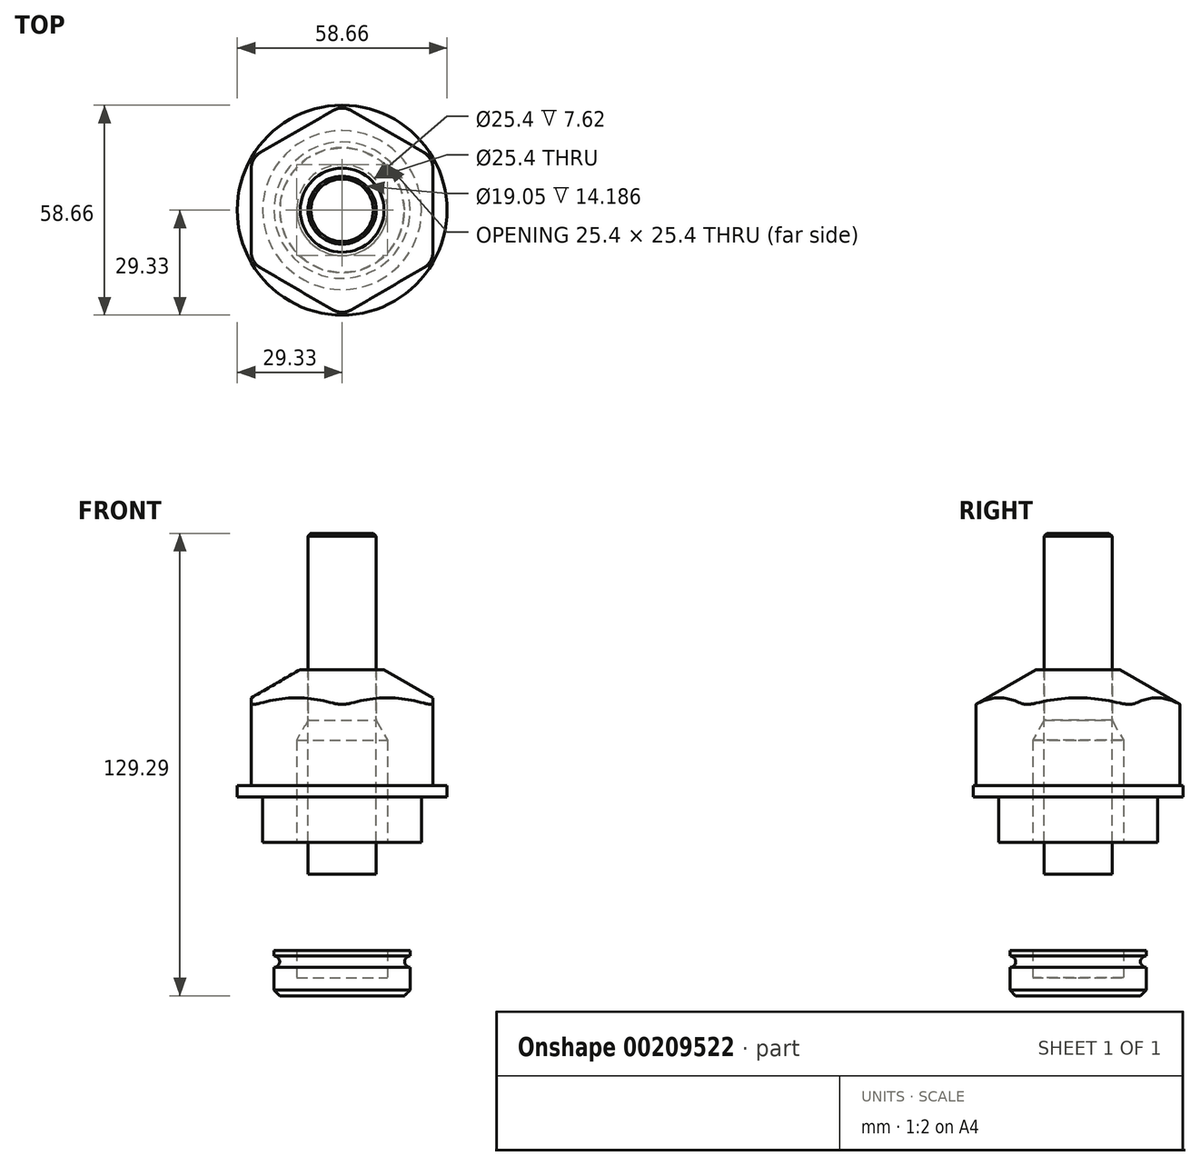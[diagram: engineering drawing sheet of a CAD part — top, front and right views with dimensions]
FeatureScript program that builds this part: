
annotation { "Feature Type Name" : "Feature", "Feature Type Description" : "" }
export const myFeature = defineFeature(function(context is Context, id is Id, definition is map)
    precondition{}
    {
        {
            var Q0;
            Q0=qCreatedBy(makeId("Top.planeOp"),FACE);
            var sketch = newSketch(context, id + "F0", { "sketchPlane" : qUnion([Q0])});
            skCircle(sketch, "E0", {"center": v(0, 0) * mm, "radius": 29.33 * mm});
            skLineSegment(sketch, "E1", {"start": v(0, 29.33) * mm, "end": v(0, -29.33) * mm, "construction": true});
            skLineSegment(sketch, "E2", {"start": v(-25.4, 14.66) * mm, "end": v(25.4, -14.66) * mm, "construction": true});
            skLineSegment(sketch, "E3", {"start": v(-25.4, -14.66) * mm, "end": v(25.4, 14.66) * mm, "construction": true});
            skLineSegment(sketch, "E4", {"start": v(-25.4, 14.66) * mm, "end": v(0, 29.33) * mm});
            skLineSegment(sketch, "E5", {"start": v(0, 29.33) * mm, "end": v(25.4, 14.66) * mm});
            skLineSegment(sketch, "E6", {"start": v(25.4, 14.66) * mm, "end": v(25.4, -14.66) * mm});
            skLineSegment(sketch, "E7", {"start": v(25.4, -14.66) * mm, "end": v(0, -29.33) * mm});
            skLineSegment(sketch, "E8", {"start": v(0, -29.33) * mm, "end": v(-25.4, -14.66) * mm});
            skLineSegment(sketch, "E9", {"start": v(-25.4, -14.66) * mm, "end": v(-25.4, 14.66) * mm});
            skCircle(sketch, "E10", {"center": v(0, 0) * mm, "radius": 7.94 * mm});
            skSolve(sketch);
        }
        {
            var Q0;
            Q0=makeQuery(id+"F0.imprint","IMPRINT",FACE,{"disambiguationData":[TD([[makeQuery(id+"F0.imprint","IMPRINT",EDGE,{"derivedFrom":sQuery(id+"F0.wireOp",EDGE,"E10")}),1.0]])]});
            var Q1;
            Q1=makeQuery(id+"F0.imprint","IMPRINT",FACE,{"disambiguationData":[TD([[makeQuery(id+"F0.imprint","IMPRINT",EDGE,{"derivedFrom":sQuery(id+"F0.wireOp",EDGE,"E4")}),-1.0]])]});
            extrude(context, id + "F1", {"entities" : qUnion([Q0, Q1]), "depth" : 35.56 * mm});
        }
        {
            var Q0;
            {var subQ0=sQuery(id+"F0.wireOp",EDGE,"E8");Q0=makeQuery(id+"F0.imprint","IMPRINT",FACE,{"disambiguationData":[TD([[makeQuery(id+"F0.imprint","IMPRINT",EDGE,{"derivedFrom":subQ0}),1.0]])]});}
            var Q1;
            {var subQ0=sQuery(id+"F0.wireOp",EDGE,"E7");Q1=makeQuery(id+"F0.imprint","IMPRINT",FACE,{"disambiguationData":[TD([[makeQuery(id+"F0.imprint","IMPRINT",EDGE,{"derivedFrom":subQ0}),1.0]])]});}
            var Q2;
            {var subQ0=sQuery(id+"F0.wireOp",EDGE,"E6");Q2=makeQuery(id+"F0.imprint","IMPRINT",FACE,{"disambiguationData":[TD([[makeQuery(id+"F0.imprint","IMPRINT",EDGE,{"derivedFrom":subQ0}),1.0]])]});}
            var Q3;
            Q3=makeQuery(id+"F0.imprint","IMPRINT",FACE,{"disambiguationData":[TD([[makeQuery(id+"F0.imprint","IMPRINT",EDGE,{"derivedFrom":sQuery(id+"F0.wireOp",EDGE,"E4")}),-1.0]])]});
            var Q4;
            {var subQ0=sQuery(id+"F0.wireOp",EDGE,"E5");Q4=makeQuery(id+"F0.imprint","IMPRINT",FACE,{"disambiguationData":[TD([[makeQuery(id+"F0.imprint","IMPRINT",EDGE,{"derivedFrom":subQ0}),1.0]])]});}
            var Q5;
            {var subQ0=sQuery(id+"F0.wireOp",EDGE,"E4");Q5=makeQuery(id+"F0.imprint","IMPRINT",FACE,{"disambiguationData":[TD([[makeQuery(id+"F0.imprint","IMPRINT",EDGE,{"derivedFrom":subQ0}),1.0]])]});}
            var Q6;
            {var subQ0=sQuery(id+"F0.wireOp",EDGE,"E9");Q6=makeQuery(id+"F0.imprint","IMPRINT",FACE,{"disambiguationData":[TD([[makeQuery(id+"F0.imprint","IMPRINT",EDGE,{"derivedFrom":subQ0}),1.0]])]});}
            extrude(context, id + "F2", {"entities" : qUnion([Q0, Q1, Q2, Q3, Q4, Q5, Q6]), "operationType" : NewBodyOperationType.ADD, "depth" : 3.17 * mm});
        }
        {
            var Q0;
            Q0=makeQuery(id+"F1.opExtrude","SWEPT_EDGE",EDGE,{"disambiguationData":[OSD([sQuery(id+"F0.wireOp",EDGE,"E0"),sQuery(id+"F0.wireOp",EDGE,"E7"),sQuery(id+"F0.wireOp",EDGE,"E8")])]});
            var Q1;
            Q1=makeQuery(id+"F1.opExtrude","SWEPT_EDGE",EDGE,{"disambiguationData":[OSD([sQuery(id+"F0.wireOp",EDGE,"E0"),sQuery(id+"F0.wireOp",EDGE,"E6"),sQuery(id+"F0.wireOp",EDGE,"E7")])]});
            var Q2;
            Q2=makeQuery(id+"F1.opExtrude","SWEPT_EDGE",EDGE,{"disambiguationData":[OSD([sQuery(id+"F0.wireOp",EDGE,"E0"),sQuery(id+"F0.wireOp",EDGE,"E5"),sQuery(id+"F0.wireOp",EDGE,"E6")])]});
            var Q3;
            Q3=makeQuery(id+"F1.opExtrude","SWEPT_EDGE",EDGE,{"disambiguationData":[OSD([sQuery(id+"F0.wireOp",EDGE,"E0"),sQuery(id+"F0.wireOp",EDGE,"E4"),sQuery(id+"F0.wireOp",EDGE,"E5")])]});
            var Q4;
            Q4=makeQuery(id+"F1.opExtrude","SWEPT_EDGE",EDGE,{"disambiguationData":[OSD([sQuery(id+"F0.wireOp",EDGE,"E0"),sQuery(id+"F0.wireOp",EDGE,"E4"),sQuery(id+"F0.wireOp",EDGE,"E9")])]});
            var Q5;
            Q5=makeQuery(id+"F1.opExtrude","SWEPT_EDGE",EDGE,{"disambiguationData":[OSD([sQuery(id+"F0.wireOp",EDGE,"E0"),sQuery(id+"F0.wireOp",EDGE,"E8"),sQuery(id+"F0.wireOp",EDGE,"E9")])]});
            fillet(context, id + "F3", {"entities" : qUnion([Q0, Q1, Q2, Q3, Q4, Q5]), "radius" : 5.08 * mm, "tangentPropagation" : true, "allowEdgeOverflow" : false});
        }
        {
            var Q0;
            Q0=qCreatedBy(makeId("Right.planeOp"),FACE);
            var sketch = newSketch(context, id + "F4", { "sketchPlane" : qUnion([Q0])});
            skLineSegment(sketch, "E11", {"start": v(0, 52) * mm, "end": v(0, 0) * mm, "construction": true});
            skLineSegment(sketch, "E12", {"start": v(11.73, 35.56) * mm, "end": v(35.4, 21.9) * mm});
            skLineSegment(sketch, "E13", {"start": v(35.4, 21.9) * mm, "end": v(35.4, 35.56) * mm});
            skLineSegment(sketch, "E14", {"start": v(35.4, 35.56) * mm, "end": v(11.73, 35.56) * mm});
            skLineSegment(sketch, "E15.0", {"start": v(11.73, 35.56) * mm, "end": v(-11.73, 35.56) * mm});
            skLineSegment(sketch, "E16.bottom", {"start": v(0, 0) * mm, "end": v(22.23, 0) * mm});
            skLineSegment(sketch, "E16.top", {"start": v(0, -12.7) * mm, "end": v(22.23, -12.7) * mm});
            skLineSegment(sketch, "E16.left", {"start": v(0, 0) * mm, "end": v(0, -12.7) * mm});
            skLineSegment(sketch, "E16.right", {"start": v(22.23, 0) * mm, "end": v(22.23, -12.7) * mm});
            skLineSegment(sketch, "E17.bottom", {"start": v(0, -12.7) * mm, "end": v(19.05, -12.7) * mm});
            skLineSegment(sketch, "E17.top", {"start": v(0, -27.69) * mm, "end": v(19.05, -27.69) * mm});
            skLineSegment(sketch, "E17.left", {"start": v(0, -12.7) * mm, "end": v(0, -27.69) * mm});
            skLineSegment(sketch, "E17.right", {"start": v(19.05, -12.7) * mm, "end": v(19.05, -27.69) * mm});
            skLineSegment(sketch, "E18.bottom", {"start": v(17.78, -27.69) * mm, "end": v(0, -27.69) * mm});
            skLineSegment(sketch, "E18.top", {"start": v(17.78, -42.93) * mm, "end": v(0, -42.93) * mm});
            skLineSegment(sketch, "E18.left", {"start": v(17.78, -27.69) * mm, "end": v(17.78, -42.93) * mm});
            skLineSegment(sketch, "E18.right", {"start": v(0, -27.69) * mm, "end": v(0, -42.93) * mm});
            skLineSegment(sketch, "E19.bottom", {"start": v(0, -42.93) * mm, "end": v(19.05, -42.93) * mm});
            skLineSegment(sketch, "E19.top", {"start": v(0, -55.63) * mm, "end": v(19.05, -55.63) * mm});
            skLineSegment(sketch, "E19.left", {"start": v(0, -42.93) * mm, "end": v(0, -55.63) * mm});
            skLineSegment(sketch, "E19.right", {"start": v(19.05, -42.93) * mm, "end": v(19.05, -55.63) * mm});
            skCircle(sketch, "E20", {"center": v(19.05, -24.51) * mm, "radius": 1.59 * mm});
            skCircle(sketch, "E21", {"center": v(19.05, -46.1) * mm, "radius": 1.59 * mm});
            skCircle(sketch, "E22", {"center": v(0, -17.46) * mm, "radius": 3.18 * mm});
            skCircle(sketch, "E23", {"center": v(0, -35.3) * mm, "radius": 3.18 * mm});
            skSolve(sketch);
        }
        {
            var Q0;
            Q0=makeQuery(id+"F4.imprint","IMPRINT",FACE,{"disambiguationData":[TD([[makeQuery(id+"F4.imprint","IMPRINT",EDGE,{"derivedFrom":sQuery(id+"F4.wireOp",EDGE,"E12")}),1.0]])]});
            var Q1;
            Q1=sQuery(id+"F4.wireOp",EDGE,"E11");
            revolve(context, id + "F5", {"operationType" : NewBodyOperationType.REMOVE, "entities" : qUnion([Q0]), "axis" : qUnion([Q1]), "revolveType" : RevolveType.FULL, "oppositeDirection" : true});
        }
        {
            var Q0;
            {var subQ7=sQuery(id+"F4.wireOp",EDGE,"E18.bottom");Q0=makeQuery(id+"F4.imprint","IMPRINT",FACE,{"disambiguationData":[TD([[makeQuery(id+"F4.imprint","IMPRINT",EDGE,{"derivedFrom":subQ7}),1.0]])]});}
            var Q1;
            {var subQ10=sQuery(id+"F4.wireOp",EDGE,"E17.bottom");Q1=makeQuery(id+"F4.imprint","IMPRINT",FACE,{"disambiguationData":[TD([[makeQuery(id+"F4.imprint","IMPRINT",EDGE,{"derivedFrom":subQ10}),-1.0]])]});}
            var Q2;
            Q2=makeQuery(id+"F4.imprint","IMPRINT",FACE,{"disambiguationData":[TD([[makeQuery(id+"F4.imprint","IMPRINT",EDGE,{"derivedFrom":sQuery(id+"F4.wireOp",EDGE,"E16.bottom")}),-1.0]])]});
            var Q3;
            {var subQ4=sQuery(id+"F4.wireOp",EDGE,"E19.top");Q3=makeQuery(id+"F4.imprint","IMPRINT",FACE,{"disambiguationData":[TD([[makeQuery(id+"F4.imprint","IMPRINT",EDGE,{"derivedFrom":subQ4}),1.0]])]});}
            var Q4;
            Q4=sQuery(id+"F4.wireOp",EDGE,"E11");
            revolve(context, id + "F6", {"operationType" : NewBodyOperationType.ADD, "entities" : qUnion([Q0, Q1, Q2, Q3]), "axis" : qUnion([Q4]), "revolveType" : RevolveType.FULL});
        }
        {
            var Q0;
            Q0=makeQuery(id+"F6.opRevolve","SWEPT_EDGE",EDGE,{"disambiguationData":[OSD([sQuery(id+"F4.wireOp",EDGE,"E19.top"),sQuery(id+"F4.wireOp",EDGE,"E19.right")])]});
            chamfer(context, id + "F7", {"entities" : qUnion([Q0]), "width" : 1.59 * mm, "tangentPropagation" : true});
        }
        {
            var Q0;
            {var subQ0=sQuery(id+"F4.wireOp",EDGE,"E16.right");var subQ1=sQuery(id+"F4.wireOp",EDGE,"E20");var subQ3=makeQuery(id+"F4.imprint","INTERSECT",VERTEX,{"disambiguationData":[OD(0.0)],"derivedFrom":[subQ0,subQ1]});Q0=makeQuery(id+"F4.imprint","IMPRINT",FACE,{"disambiguationData":[TD([[makeQuery(id+"F4.imprint","SKETCH_ENTITY",EDGE,{"disambiguationData":[TD([[subQ3,-1.0]])],"sketchEntityId":"E16.right"}),1.0]])]});}
            var Q1;
            {var subQ0=sQuery(id+"F4.wireOp",EDGE,"E20");var subQ1=sQuery(id+"F4.wireOp",EDGE,"E17.right");var subQ3=makeQuery(id+"F4.imprint","INTERSECT",VERTEX,{"disambiguationData":[OD(0.0)],"derivedFrom":[subQ1,subQ0]});Q1=makeQuery(id+"F4.imprint","IMPRINT",FACE,{"disambiguationData":[TD([[makeQuery(id+"F4.imprint","IMPRINT",EDGE,{"disambiguationData":[TD([[subQ3,-1.0]])],"derivedFrom":subQ1}),-1.0]])]});}
            var Q2;
            {var subQ0=sQuery(id+"F4.wireOp",EDGE,"E20");var subQ1=sQuery(id+"F4.wireOp",EDGE,"E17.right");var subQ3=makeQuery(id+"F4.imprint","INTERSECT",VERTEX,{"disambiguationData":[OD(0.0)],"derivedFrom":[subQ1,subQ0]});Q2=makeQuery(id+"F4.imprint","IMPRINT",FACE,{"disambiguationData":[TD([[makeQuery(id+"F4.imprint","IMPRINT",EDGE,{"disambiguationData":[TD([[subQ3,-1.0]])],"derivedFrom":subQ1}),1.0]])]});}
            var Q3;
            Q3=sQuery(id+"F4.wireOp",EDGE,"E11");
            revolve(context, id + "F8", {"entities" : qUnion([Q0, Q1, Q2]), "axis" : qUnion([Q3]), "revolveType" : RevolveType.FULL});
        }
        {
            var Q0;
            {var subQ0=sQuery(id+"F4.wireOp",EDGE,"E22");var subQ1=sQuery(id+"F4.wireOp",EDGE,"E17.left");var subQ3=makeQuery(id+"F4.imprint","INTERSECT",VERTEX,{"disambiguationData":[OD(0.0)],"derivedFrom":[subQ1,subQ0]});Q0=makeQuery(id+"F4.imprint","IMPRINT",FACE,{"disambiguationData":[TD([[makeQuery(id+"F4.imprint","IMPRINT",EDGE,{"disambiguationData":[TD([[subQ3,-1.0]])],"derivedFrom":subQ1}),-1.0]])]});}
            var Q1;
            {var subQ0=sQuery(id+"F4.wireOp",EDGE,"E22");var subQ1=sQuery(id+"F4.wireOp",EDGE,"E17.left");var subQ3=makeQuery(id+"F4.imprint","INTERSECT",VERTEX,{"disambiguationData":[OD(0.0)],"derivedFrom":[subQ1,subQ0]});Q1=makeQuery(id+"F4.imprint","IMPRINT",FACE,{"disambiguationData":[TD([[makeQuery(id+"F4.imprint","IMPRINT",EDGE,{"disambiguationData":[TD([[subQ3,-1.0]])],"derivedFrom":subQ1}),1.0]])]});}
            var Q2;
            {var subQ0=sQuery(id+"F4.wireOp",EDGE,"E23");var subQ1=sQuery(id+"F4.wireOp",EDGE,"E18.right");var subQ3=makeQuery(id+"F4.imprint","INTERSECT",VERTEX,{"disambiguationData":[OD(0.0)],"derivedFrom":[subQ1,subQ0]});Q2=makeQuery(id+"F4.imprint","IMPRINT",FACE,{"disambiguationData":[TD([[makeQuery(id+"F4.imprint","IMPRINT",EDGE,{"disambiguationData":[TD([[subQ3,-1.0]])],"derivedFrom":subQ1}),-1.0]])]});}
            var Q3;
            {var subQ0=sQuery(id+"F4.wireOp",EDGE,"E23");var subQ1=sQuery(id+"F4.wireOp",EDGE,"E18.right");var subQ3=makeQuery(id+"F4.imprint","INTERSECT",VERTEX,{"disambiguationData":[OD(0.0)],"derivedFrom":[subQ1,subQ0]});Q3=makeQuery(id+"F4.imprint","IMPRINT",FACE,{"disambiguationData":[TD([[makeQuery(id+"F4.imprint","IMPRINT",EDGE,{"disambiguationData":[TD([[subQ3,-1.0]])],"derivedFrom":subQ1}),1.0]])]});}
            extrude(context, id + "F9", {"entities" : qUnion([Q0, Q1, Q2, Q3]), "operationType" : NewBodyOperationType.REMOVE, "endBound" : BoundingType.THROUGH_ALL, "depth" : 25.4 * mm});
        }
        {
            var Q0;
            Q0=qCreatedBy(makeId("Right.planeOp"),FACE);
            var sketch = newSketch(context, id + "F10", { "sketchPlane" : qUnion([Q0])});
            skLineSegment(sketch, "E24", {"start": v(0, 73.66) * mm, "end": v(0, -50.55) * mm});
            skLineSegment(sketch, "E25", {"start": v(0, -50.55) * mm, "end": v(12.7, -50.55) * mm});
            skLineSegment(sketch, "E26", {"start": v(12.7, -50.55) * mm, "end": v(12.7, 15.88) * mm});
            skLineSegment(sketch, "E27", {"start": v(12.7, 15.88) * mm, "end": v(0, 15.88) * mm});
            skLineSegment(sketch, "E28", {"start": v(9.53, -21.6) * mm, "end": v(9.53, 73.66) * mm});
            skLineSegment(sketch, "E29", {"start": v(9.52, 73.66) * mm, "end": v(0, 73.66) * mm});
            skLineSegment(sketch, "E30", {"start": v(9.53, 21.37) * mm, "end": v(12.7, 15.88) * mm});
            skLineSegment(sketch, "E31.rect.bottom", {"start": v(12.7, -27.94) * mm, "end": v(-12.7, -27.94) * mm});
            skLineSegment(sketch, "E31.rect.top", {"start": v(12.7, -21.59) * mm, "end": v(-12.7, -21.59) * mm});
            skLineSegment(sketch, "E31.rect.left", {"start": v(12.7, -27.94) * mm, "end": v(12.7, -21.59) * mm});
            skLineSegment(sketch, "E31.rect.right", {"start": v(-12.7, -27.94) * mm, "end": v(-12.7, -21.59) * mm});
            skPoint(sketch, "E31.rect.middle", {"position": v(0, -24.77) * mm});
            skSolve(sketch);
        }
        {
            var Q0;
            {var subQ0=sQuery(id+"F10.wireOp",EDGE,"E29");Q0=makeQuery(id+"F10.imprint","IMPRINT",FACE,{"disambiguationData":[TD([[makeQuery(id+"F10.imprint","IMPRINT",EDGE,{"derivedFrom":subQ0}),1.0]])]});}
            var Q1;
            {var subQ0=sQuery(id+"F10.wireOp",EDGE,"E30");Q1=makeQuery(id+"F10.imprint","IMPRINT",FACE,{"disambiguationData":[TD([[makeQuery(id+"F10.imprint","IMPRINT",EDGE,{"derivedFrom":subQ0}),-1.0]])]});}
            var Q2;
            {var subQ1=sQuery(id+"F10.wireOp",EDGE,"E24");var subQ5=sQuery(id+"F10.wireOp",EDGE,"E27");var subQ7=makeQuery(id+"F10.imprint","INTERSECT",VERTEX,{"derivedFrom":[subQ1,subQ5]});Q2=makeQuery(id+"F10.imprint","IMPRINT",FACE,{"disambiguationData":[TD([[makeQuery(id+"F10.imprint","IMPRINT",EDGE,{"disambiguationData":[TD([[subQ7,-1.0]])],"derivedFrom":subQ1}),1.0]])]});}
            var Q3;
            {var subQ0=sQuery(id+"F10.wireOp",EDGE,"E31.rect.top");var subQ3=sQuery(id+"F10.wireOp",EDGE,"E28");var subQ4=makeQuery(id+"F10.imprint","INTERSECT",VERTEX,{"derivedFrom":[subQ3,subQ0]});Q3=makeQuery(id+"F10.imprint","IMPRINT",FACE,{"disambiguationData":[TD([[makeQuery(id+"F10.imprint","IMPRINT",EDGE,{"disambiguationData":[TD([[subQ4,-1.0]])],"derivedFrom":subQ3}),-1.0]])]});}
            var Q4;
            {var subQ5=sQuery(id+"F10.wireOp",EDGE,"E25");Q4=makeQuery(id+"F10.imprint","IMPRINT",FACE,{"disambiguationData":[TD([[makeQuery(id+"F10.imprint","IMPRINT",EDGE,{"derivedFrom":subQ5}),1.0]])]});}
            var Q5;
            {var subQ0=sQuery(id+"F10.wireOp",EDGE,"E31.rect.left");Q5=makeQuery(id+"F10.imprint","IMPRINT",FACE,{"disambiguationData":[TD([[makeQuery(id+"F10.imprint","IMPRINT",EDGE,{"derivedFrom":subQ0}),1.0]])]});}
            var Q6;
            Q6=sQuery(id+"F10.wireOp",EDGE,"E24");
            revolve(context, id + "F11", {"operationType" : NewBodyOperationType.REMOVE, "entities" : qUnion([Q0, Q1, Q2, Q3, Q4, Q5]), "axis" : qUnion([Q6]), "revolveType" : RevolveType.FULL, "oppositeDirection" : true});
        }
        {
            var Q0;
            {var subQ0=sQuery(id+"F10.wireOp",EDGE,"E29");Q0=makeQuery(id+"F10.imprint","IMPRINT",FACE,{"disambiguationData":[TD([[makeQuery(id+"F10.imprint","IMPRINT",EDGE,{"derivedFrom":subQ0}),1.0]])]});}
            var Q1;
            {var subQ1=sQuery(id+"F10.wireOp",EDGE,"E24");var subQ5=sQuery(id+"F10.wireOp",EDGE,"E27");var subQ7=makeQuery(id+"F10.imprint","INTERSECT",VERTEX,{"derivedFrom":[subQ1,subQ5]});Q1=makeQuery(id+"F10.imprint","IMPRINT",FACE,{"disambiguationData":[TD([[makeQuery(id+"F10.imprint","IMPRINT",EDGE,{"disambiguationData":[TD([[subQ7,-1.0]])],"derivedFrom":subQ1}),1.0]])]});}
            var Q2;
            {var subQ0=sQuery(id+"F10.wireOp",EDGE,"E31.rect.left");Q2=makeQuery(id+"F10.imprint","IMPRINT",FACE,{"disambiguationData":[TD([[makeQuery(id+"F10.imprint","IMPRINT",EDGE,{"derivedFrom":subQ0}),1.0]])]});}
            var Q3;
            Q3=sQuery(id+"F10.wireOp",EDGE,"E24");
            revolve(context, id + "F12", {"entities" : qUnion([Q0, Q1, Q2]), "axis" : qUnion([Q3]), "revolveType" : RevolveType.FULL});
        }
        {
            var Q0;
            Q0=makeQuery(id+"F12.opRevolve","SWEPT_EDGE",EDGE,{"disambiguationData":[OSD([sQuery(id+"F10.wireOp",EDGE,"E28"),sQuery(id+"F10.wireOp",EDGE,"E29")])]});
            chamfer(context, id + "F13", {"entities" : qUnion([Q0]), "width" : 0.8 * mm, "tangentPropagation" : true});
        }
    });
